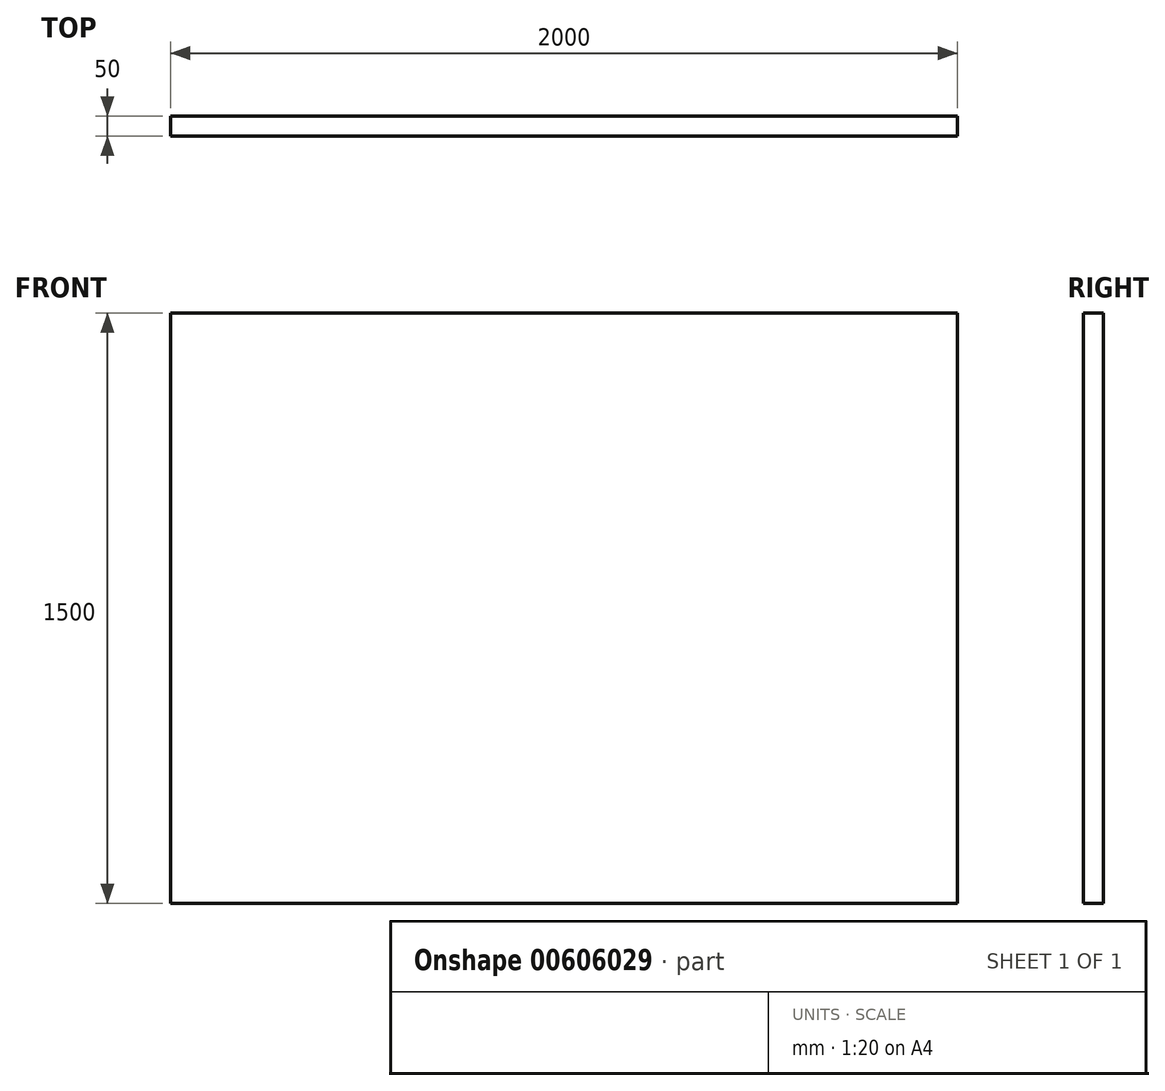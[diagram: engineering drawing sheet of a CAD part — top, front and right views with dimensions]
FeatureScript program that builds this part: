
annotation { "Feature Type Name" : "Feature", "Feature Type Description" : "" }
export const myFeature = defineFeature(function(context is Context, id is Id, definition is map)
    precondition{}
    {
        {
            var Q0;
            Q0=qCreatedBy(makeId("Front.planeOp"),FACE);
            var sketch = newSketch(context, id + "F0", { "sketchPlane" : qUnion([Q0])});
            skLineSegment(sketch, "E0.bottom", {"start": v(1000, 750) * mm, "end": v(-1000, 750) * mm});
            skLineSegment(sketch, "E0.top", {"start": v(1000, -750) * mm, "end": v(-1000, -750) * mm});
            skLineSegment(sketch, "E0.left", {"start": v(1000, 750) * mm, "end": v(1000, -750) * mm});
            skLineSegment(sketch, "E0.right", {"start": v(-1000, 750) * mm, "end": v(-1000, -750) * mm});
            skPoint(sketch, "E0.middle", {"position": v(0, 0) * mm});
            skSolve(sketch);
        }
        {
            var Q0;
            Q0=makeQuery(id+"F0.imprint","IMPRINT",FACE,{"disambiguationData":[TD([[makeQuery(id+"F0.imprint","IMPRINT",EDGE,{"derivedFrom":sQuery(id+"F0.wireOp",EDGE,"E0.bottom")}),1.0]])]});
            extrude(context, id + "F1", {"entities" : qUnion([Q0]), "depth" : 50 * mm, "offsetDistance" : 25.4 * mm});
        }
    });
